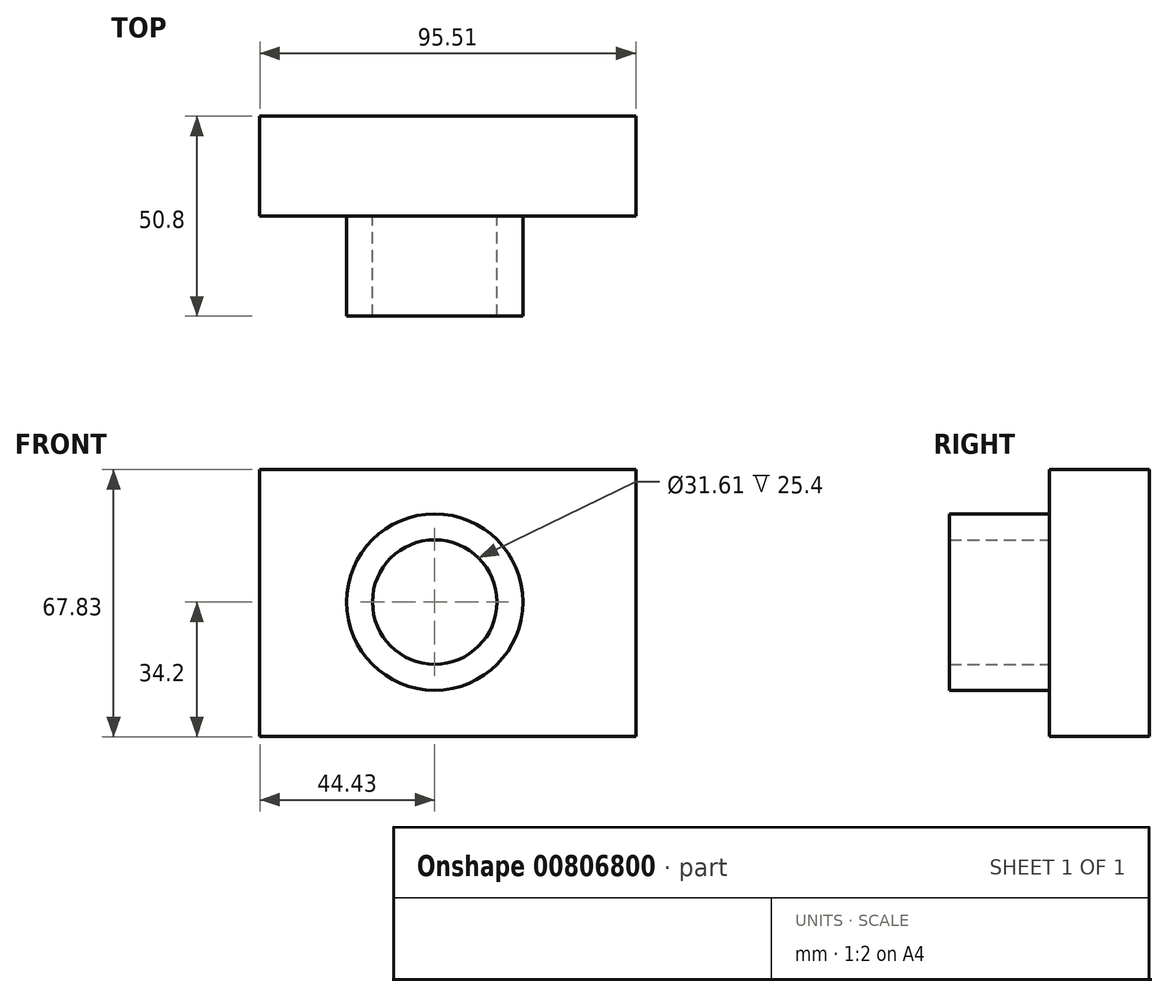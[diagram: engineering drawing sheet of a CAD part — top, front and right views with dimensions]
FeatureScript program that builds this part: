
annotation { "Feature Type Name" : "Feature", "Feature Type Description" : "" }
export const myFeature = defineFeature(function(context is Context, id is Id, definition is map)
    precondition{}
    {
        {
            var Q0;
            Q0=qCreatedBy(makeId("Front.planeOp"),FACE);
            var sketch = newSketch(context, id + "F0", { "sketchPlane" : qUnion([Q0])});
            skCircle(sketch, "E0", {"center": v(0, 0) * mm, "radius": 22.4 * mm});
            skCircle(sketch, "E1", {"center": v(0, 0) * mm, "radius": 15.8 * mm});
            skSolve(sketch);
        }
        {
            var Q0;
            Q0=makeQuery(id+"F0.imprint","IMPRINT",FACE,{"disambiguationData":[TD([[makeQuery(id+"F0.imprint","IMPRINT",EDGE,{"derivedFrom":sQuery(id+"F0.wireOp",EDGE,"E0")}),1.0]])]});
            extrude(context, id + "F1", {"entities" : qUnion([Q0]), "depth" : 50.8 * mm, "offsetDistance" : 25.4 * mm});
        }
        {
            var Q0;
            Q0=qCreatedBy(makeId("Front.planeOp"),FACE);
            var sketch = newSketch(context, id + "F2", { "sketchPlane" : qUnion([Q0])});
            skLineSegment(sketch, "E2.bottom", {"start": v(-44.43, 33.63) * mm, "end": v(51.08, 33.63) * mm});
            skLineSegment(sketch, "E2.top", {"start": v(-44.43, -34.2) * mm, "end": v(51.08, -34.2) * mm});
            skLineSegment(sketch, "E2.left", {"start": v(-44.43, 33.63) * mm, "end": v(-44.43, -34.2) * mm});
            skLineSegment(sketch, "E2.right", {"start": v(51.08, 33.63) * mm, "end": v(51.08, -34.2) * mm});
            skSolve(sketch);
        }
        {
            var Q0;
            Q0 = qSketchRegion(id + "F2", true);
            extrude(context, id + "F3", {"entities" : qUnion([Q0]), "operationType" : NewBodyOperationType.ADD, "depth" : 25.4 * mm, "offsetDistance" : 25.4 * mm});
        }
    });
